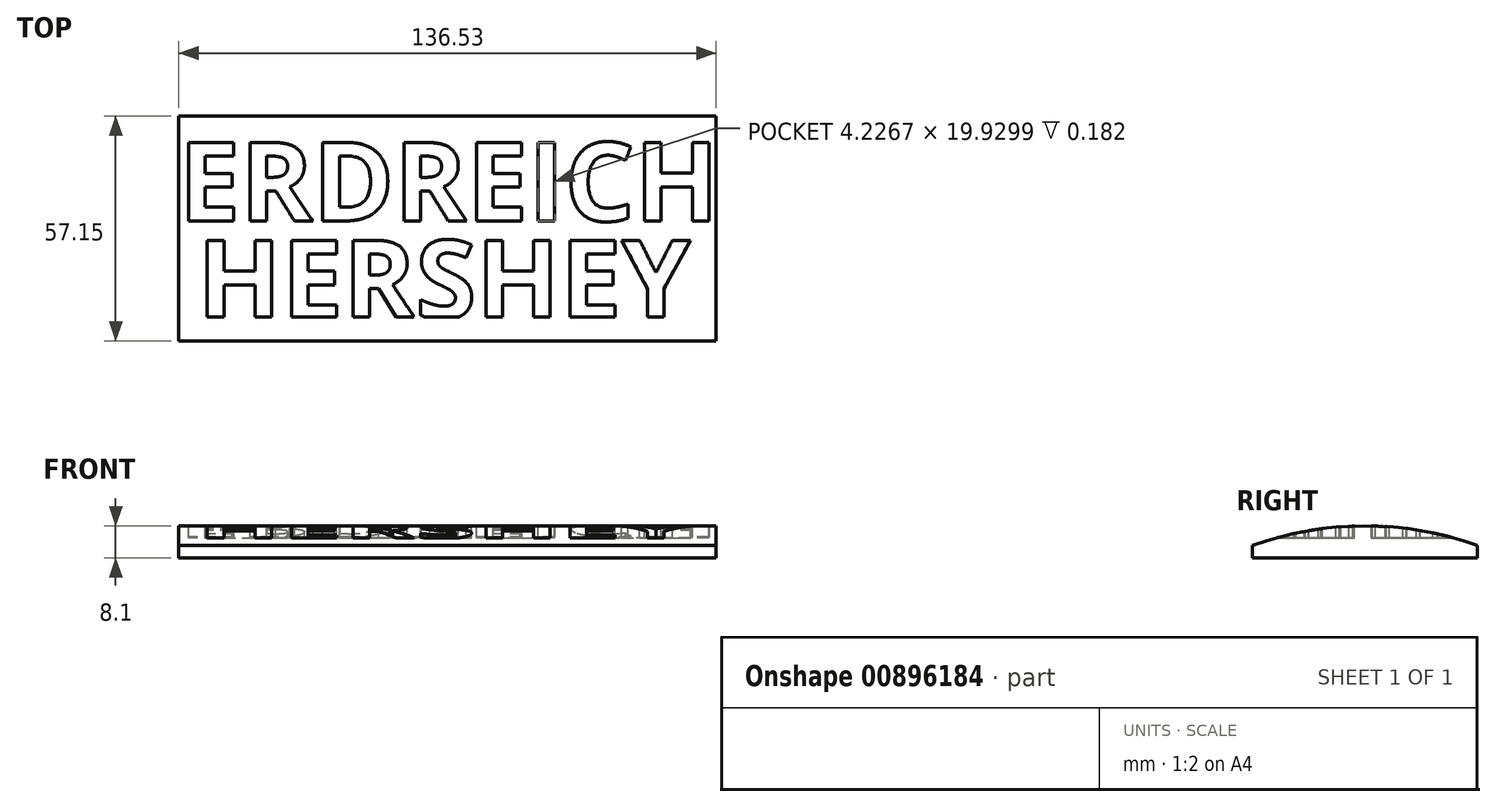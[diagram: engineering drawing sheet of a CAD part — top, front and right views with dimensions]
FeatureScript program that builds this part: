
annotation { "Feature Type Name" : "Feature", "Feature Type Description" : "" }
export const myFeature = defineFeature(function(context is Context, id is Id, definition is map)
    precondition{}
    {
        {
            var Q0;
            Q0=qCreatedBy(makeId("Top.planeOp"),FACE);
            var sketch = newSketch(context, id + "F0", { "sketchPlane" : qUnion([Q0])});
            skLineSegment(sketch, "E0.bottom", {"start": v(0, 0) * mm, "end": v(136.53, 0) * mm});
            skLineSegment(sketch, "E0.top", {"start": v(0, 57.15) * mm, "end": v(136.53, 57.15) * mm});
            skLineSegment(sketch, "E0.left", {"start": v(0, 0) * mm, "end": v(0, 57.15) * mm});
            skLineSegment(sketch, "E0.right", {"start": v(136.53, 0) * mm, "end": v(136.53, 57.15) * mm});
            skSolve(sketch);
        }
        {
            var Q0;
            Q0=makeQuery(id+"F0.imprint","IMPRINT",FACE,{"disambiguationData":[TD([[makeQuery(id+"F0.imprint","IMPRINT",EDGE,{"derivedFrom":sQuery(id+"F0.wireOp",EDGE,"E0.bottom")}),1.0]])]});
            extrude(context, id + "F1", {"entities" : qUnion([Q0]), "depth" : 3.17 * mm, "offsetDistance" : 25.4 * mm});
        }
        {
            var Q0;
            Q0=qCreatedBy(makeId("Right.planeOp"),FACE);
            var sketch = newSketch(context, id + "F2", { "sketchPlane" : qUnion([Q0])});
            skArc(sketch, "E1", {"start": v(57.15, 3.18) * mm, "mid": v(28.57, 8.1) * mm, "end": v(0, 3.16) * mm});
            skLineSegment(sketch, "E2", {"start": v(57.15, 3.18) * mm, "end": v(55.14, 1.86) * mm});
            skLineSegment(sketch, "E3", {"start": v(55.14, 1.86) * mm, "end": v(1.3, 1.86) * mm});
            skLineSegment(sketch, "E4", {"start": v(1.3, 1.86) * mm, "end": v(0, 3.16) * mm});
            skSolve(sketch);
        }
        {
            var Q0;
            Q0=makeQuery(id+"F2.imprint","IMPRINT",FACE,{"disambiguationData":[TD([[makeQuery(id+"F2.imprint","IMPRINT",EDGE,{"derivedFrom":sQuery(id+"F2.wireOp",EDGE,"E1")}),1.0]])]});
            extrude(context, id + "F3", {"entities" : qUnion([Q0]), "operationType" : NewBodyOperationType.ADD, "depth" : 136.53 * mm, "offsetDistance" : 25.4 * mm});
        }
        {
            var Q0;
            Q0=qCreatedBy(makeId("Top.planeOp"),FACE);
            cPlane(context, id + "F4", {"entities" : qUnion([Q0]), "cplaneType" : CPlaneType.OFFSET, "offset" : 8.9 * mm, "width" : 152.4 * mm, "height" : 152.4 * mm});
        }
        {
            var Q0;
            Q0=qCreatedBy(id+"F4.planeOp",FACE);
            var sketch = newSketch(context, id + "F5", { "sketchPlane" : qUnion([Q0])});
            skText(sketch, "E5", { "text": "ERDREICH", "fontName": "OpenSans-Bold.ttf"});
            skText(sketch, "E6", { "text": "HERSHEY\n", "fontName": "OpenSans-Bold.ttf"});
            const initialGuessF5  = {"E5": [0, 0.0305, 1, 0, 0.0201], "E6": [0.00473, 0.00563, 1, 0, 0.0201]};
            skSetInitialGuess(sketch, initialGuessF5);
            skSolve(sketch);
        }
        {
            var Q0;
            Q0 = qSketchRegion(id + "F5", true);
            extrude(context, id + "F6", {"entities" : qUnion([Q0]), "operationType" : NewBodyOperationType.REMOVE, "oppositeDirection" : true, "depth" : 3.8 * mm, "offsetDistance" : 25.4 * mm});
        }
    });
